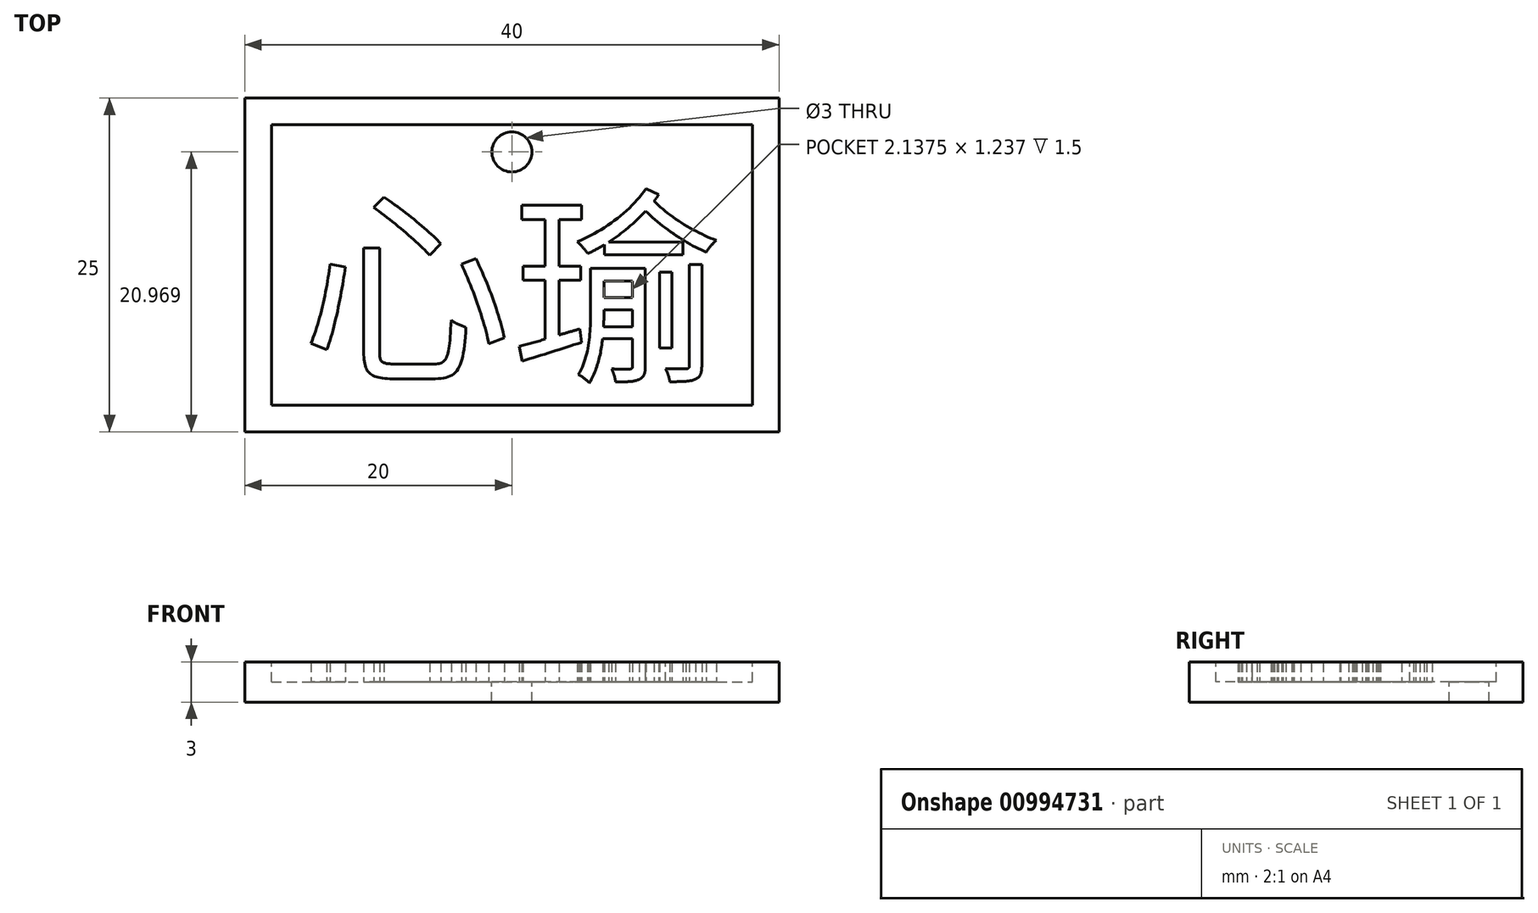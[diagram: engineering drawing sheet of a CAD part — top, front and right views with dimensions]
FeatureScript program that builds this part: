
annotation { "Feature Type Name" : "Feature", "Feature Type Description" : "" }
export const myFeature = defineFeature(function(context is Context, id is Id, definition is map)
    precondition{}
    {
        {
            var Q0;
            Q0=qCreatedBy(makeId("Top.planeOp"),FACE);
            var sketch = newSketch(context, id + "F0", { "sketchPlane" : qUnion([Q0])});
            skLineSegment(sketch, "E0.bottom", {"start": v(20, 12.5) * mm, "end": v(-20, 12.5) * mm});
            skLineSegment(sketch, "E0.top", {"start": v(20, -12.5) * mm, "end": v(-20, -12.5) * mm});
            skLineSegment(sketch, "E0.left", {"start": v(20, 12.5) * mm, "end": v(20, -12.5) * mm});
            skLineSegment(sketch, "E0.right", {"start": v(-20, 12.5) * mm, "end": v(-20, -12.5) * mm});
            skPoint(sketch, "E0.middle", {"position": v(0, 0) * mm});
            skSolve(sketch);
        }
        {
            var Q0;
            Q0 = qSketchRegion(id + "F0", true);
            extrude(context, id + "F1", {"entities" : qUnion([Q0]), "depth" : 3 * mm, "offsetDistance" : 25 * mm});
        }
        {
            var Q0;
            Q0=makeQuery(id+"F1.opExtrude","CAP_FACE",FACE,{"disambiguationData":[OSD([sQuery(id+"F0.wireOp",EDGE,"E0.bottom"),sQuery(id+"F0.wireOp",EDGE,"E0.top"),sQuery(id+"F0.wireOp",EDGE,"E0.left"),sQuery(id+"F0.wireOp",EDGE,"E0.right")])],"isStart":false});
            var sketch = newSketch(context, id + "F2", { "sketchPlane" : qUnion([Q0])});
            skLineSegment(sketch, "E1.0", {"start": v(-18, -10.5) * mm, "end": v(18, -10.5) * mm});
            skLineSegment(sketch, "E1.1", {"start": v(-18, 10.5) * mm, "end": v(-18, -10.5) * mm});
            skLineSegment(sketch, "E1.2", {"start": v(18, 10.5) * mm, "end": v(-18, 10.5) * mm});
            skLineSegment(sketch, "E1.3", {"start": v(18, -10.5) * mm, "end": v(18, 10.5) * mm});
            skSolve(sketch);
        }
        {
            var Q0;
            Q0 = qSketchRegion(id + "F2", true);
            extrude(context, id + "F3", {"entities" : qUnion([Q0]), "operationType" : NewBodyOperationType.REMOVE, "oppositeDirection" : true, "depth" : 1.5 * mm, "offsetDistance" : 25 * mm});
        }
        {
            var Q0;
            Q0=makeQuery(id+"F3.boolean.opBoolean","COPY",FACE,{"derivedFrom":makeQuery(id+"F3.opExtrude","CAP_FACE",FACE,{"disambiguationData":[OSD([sQuery(id+"F2.wireOp",EDGE,"E1.0"),sQuery(id+"F2.wireOp",EDGE,"E1.1"),sQuery(id+"F2.wireOp",EDGE,"E1.2"),sQuery(id+"F2.wireOp",EDGE,"E1.3")])],"isStart":false})});
            var sketch = newSketch(context, id + "F4", { "sketchPlane" : qUnion([Q0])});
            skCircle(sketch, "E2", {"center": v(0, 8.47) * mm, "radius": 1.5 * mm});
            skSolve(sketch);
        }
        {
            var Q0;
            Q0 = qSketchRegion(id + "F4", true);
            extrude(context, id + "F5", {"entities" : qUnion([Q0]), "operationType" : NewBodyOperationType.REMOVE, "endBound" : BoundingType.THROUGH_ALL, "oppositeDirection" : true, "depth" : 25 * mm, "offsetDistance" : 25 * mm});
        }
        {
            var Q0;
            Q0=makeQuery(id+"F3.boolean.opBoolean","COPY",FACE,{"derivedFrom":makeQuery(id+"F3.opExtrude","CAP_FACE",FACE,{"disambiguationData":[OSD([sQuery(id+"F2.wireOp",EDGE,"E1.0"),sQuery(id+"F2.wireOp",EDGE,"E1.1"),sQuery(id+"F2.wireOp",EDGE,"E1.2"),sQuery(id+"F2.wireOp",EDGE,"E1.3")])],"isStart":false})});
            var sketch = newSketch(context, id + "F6", { "sketchPlane" : qUnion([Q0])});
            skText(sketch, "E3", { "text": "心瑜", "fontName": "NotoSansCJKtc-Regular.otf"});
            const initialGuessF6  = {"E3": [-0.0158, -0.00761, 1, 0, 0.0114]};
            skSetInitialGuess(sketch, initialGuessF6);
            skSolve(sketch);
        }
        {
            var Q0;
            Q0 = qSketchRegion(id + "F6", true);
            extrude(context, id + "F7", {"entities" : qUnion([Q0]), "operationType" : NewBodyOperationType.ADD, "depth" : 1.5 * mm, "offsetDistance" : 25 * mm});
        }
    });
